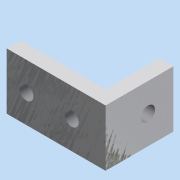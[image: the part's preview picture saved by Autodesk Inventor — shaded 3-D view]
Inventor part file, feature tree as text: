
AUTODESK INVENTOR PART (.ipt)
format: ipt  version: 2015 (Build 190159000, 159)  size: 115,712 bytes
history: native  units: mm
features: sketch x3, hole x2, extrude x1
ambient origin geometry x8: Origin, YZ Plane, XZ Plane, XY Plane, X Axis, Y Axis, Z Axis, Center Point
bodies: Solid1 (feature_tree)
feature tree (6):
  extrude  "Extrusion1"  Depth=5.0mm
  hole  "Hole1"  [1 undecoded]
  hole  "Hole2"  [1 undecoded]
  sketch  "Sketch1"  dims[d0=5.0mm d1=5.0mm]
  sketch  "Sketch2"  dims[d2=35.0mm d3=19.0mm]
  sketch  "Sketch3"  dims[d4=20.0mm d5=0.0mm d6=10.0mm d7=7.0mm d8=7.0mm d9=5.0mm d10=6.0mm d11=4.0mm d12=2.0mm d13=90.0deg d14=8.0mm d15=20.594885mm d18=10.0mm d19=10.0mm d20=5.0mm d21=6.0mm d22=4.0mm d23=2.0mm d24=90.0deg d25=8.0mm d26=20.594885mm]
note: 2 required parameter values undecoded (feature->parameter linkage not recoverable at this tier; creation-order binding heuristic only, values carry confidence <= 0.55)
